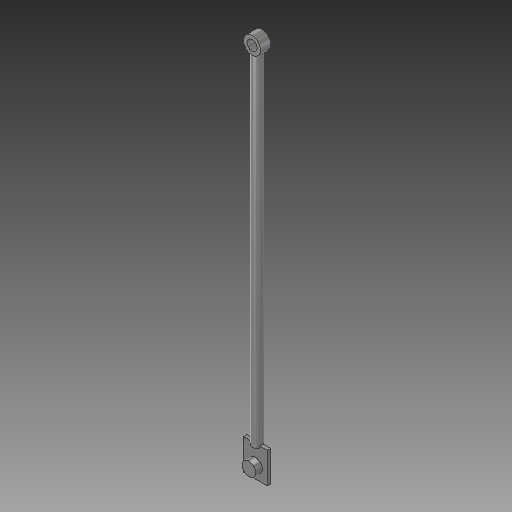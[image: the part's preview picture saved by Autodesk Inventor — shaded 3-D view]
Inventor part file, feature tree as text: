
AUTODESK INVENTOR PART (.ipt)
format: ipt  version: 2019 (Build 230136000, 136)  size: 145,920 bytes
history: native  units: mm
features: sketch x6, extrude x4, plane x2, revolve x1
ambient origin geometry x8: Origin, YZ Plane, XZ Plane, XY Plane, X Axis, Y Axis, Z Axis, Center Point
bodies: Solid1 (feature_tree)
feature tree (13):
  extrude  "Extrusion1"  Depth=100.0mm TaperAngle=0.0deg
  plane  "Work Plane1"
  sketch  "Sketch2"  dims[d3=-0.5mm d4=1.5mm]
  revolve  "Revolution1"  [1 undecoded]
  plane  "Work Plane2"
  extrude  "Extrusion2"  Depth=1.0mm
  extrude  "Extrusion3"  TaperAngle=90.0deg  [1 undecoded]
  extrude  "Extrusion4"  Depth=3.5mm
  sketch  "Sketch1"  dims[d0=2.8mm d1=100.0mm d2=0.0mm]
  sketch  "Sketch3"  dims[d5=1.5mm d6=1.0mm]
  sketch  "Sketch4"  dims[d7=2.5mm d8=90.0deg]
  sketch  "Sketch5"  dims[d9=-0.5mm d12=3.5mm]
  sketch  "Sketch6"  dims[d13=1.0mm d14=9.0mm d15=0.0mm d16=3.5mm d17=4.0mm d18=1.2mm d19=0.0mm d20=1.9mm d21=0.0mm]
note: 2 required parameter values undecoded (feature->parameter linkage not recoverable at this tier; creation-order binding heuristic only, values carry confidence <= 0.55)